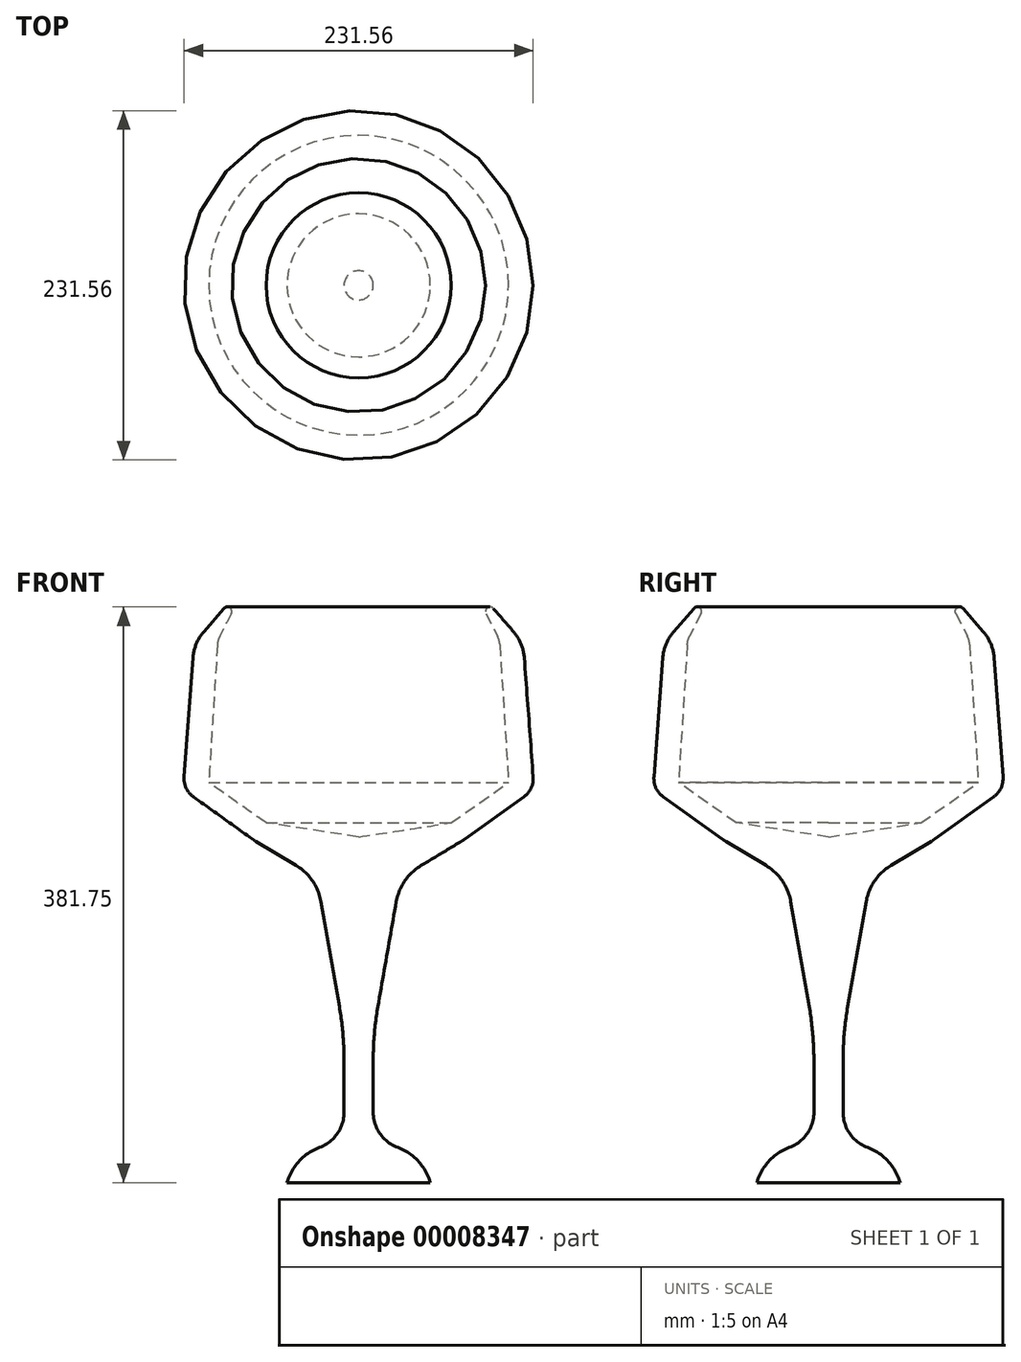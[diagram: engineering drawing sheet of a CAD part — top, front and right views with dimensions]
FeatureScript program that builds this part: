
annotation { "Feature Type Name" : "Feature", "Feature Type Description" : "" }
export const myFeature = defineFeature(function(context is Context, id is Id, definition is map)
    precondition{}
    {
        {
            var Q0;
            Q0=qCreatedBy(makeId("Right.planeOp"),FACE);
            var sketch = newSketch(context, id + "F0", { "sketchPlane" : qUnion([Q0])});
            skLineSegment(sketch, "E0", {"start": v(-9.68, 0) * mm, "end": v(-9.68, -77.4) * mm});
            skLineSegment(sketch, "E1", {"start": v(-9.68, -77.4) * mm, "end": v(-47.46, -77.4) * mm});
            skLineSegment(sketch, "E2", {"start": v(-47.46, -77.4) * mm, "end": v(-47.46, -99.1) * mm});
            skLineSegment(sketch, "E3", {"start": v(-47.46, -99.1) * mm, "end": v(0, -99.1) * mm});
            skLineSegment(sketch, "E4", {"start": v(0, -99.1) * mm, "end": v(0, 130.1) * mm});
            skLineSegment(sketch, "E5", {"start": v(0, 130.1) * mm, "end": v(-61.35, 139.5) * mm});
            skLineSegment(sketch, "E6", {"start": v(-61.35, 139.5) * mm, "end": v(-99.4, 166.13) * mm});
            skLineSegment(sketch, "E7", {"start": v(-99.4, 166.13) * mm, "end": v(-93.44, 260.67) * mm});
            skLineSegment(sketch, "E8", {"start": v(-93.44, 260.67) * mm, "end": v(-73.2, 300.3) * mm});
            skLineSegment(sketch, "E9", {"start": v(-73.2, 300.3) * mm, "end": v(-109.12, 258.83) * mm});
            skLineSegment(sketch, "E10", {"start": v(-109.12, 258.83) * mm, "end": v(-116.36, 161.57) * mm});
            skLineSegment(sketch, "E11", {"start": v(-116.36, 161.57) * mm, "end": v(-69.34, 127.9) * mm});
            skLineSegment(sketch, "E12", {"start": v(-69.34, 127.9) * mm, "end": v(-27.73, 102.92) * mm});
            skLineSegment(sketch, "E13", {"start": v(-27.73, 102.92) * mm, "end": v(-9.68, 0) * mm});
            skLineSegment(sketch, "E14", {"start": v(-47.46, -77.4) * mm, "end": v(-119.56, -99.1) * mm});
            skLineSegment(sketch, "E15", {"start": v(-119.56, -99.1) * mm, "end": v(-47.46, -99.1) * mm});
            skSolve(sketch);
        }
        {
            var Q0;
            Q0=makeQuery(id+"F0.imprint","IMPRINT",FACE,{"disambiguationData":[TD([[makeQuery(id+"F0.imprint","IMPRINT",EDGE,{"derivedFrom":sQuery(id+"F0.wireOp",EDGE,"E0")}),1.0]])]});
            var Q1;
            Q1=sQuery(id+"F0.wireOp",EDGE,"E4");
            revolve(context, id + "F1", {"entities" : qUnion([Q0]), "axis" : qUnion([Q1]), "revolveType" : RevolveType.FULL});
        }
        {
            var Q0;
            Q0=makeQuery(id+"F1.opRevolve","SWEPT_EDGE",EDGE,{"disambiguationData":[OSD([sQuery(id+"F0.wireOp",EDGE,"E8"),sQuery(id+"F0.wireOp",EDGE,"E9")])]});
            fillet(context, id + "F2", {"entities" : qUnion([Q0]), "radius" : 3 * mm, "allowEdgeOverflow" : false});
        }
        {
            var Q0;
            Q0=makeQuery(id+"F1.opRevolve","SWEPT_EDGE",EDGE,{"disambiguationData":[OSD([sQuery(id+"F0.wireOp",EDGE,"E9"),sQuery(id+"F0.wireOp",EDGE,"E10")])]});
            fillet(context, id + "F3", {"entities" : qUnion([Q0]), "radius" : 30 * mm, "allowEdgeOverflow" : false});
        }
        {
            var Q0;
            Q0=makeQuery(id+"F1.opRevolve","SWEPT_EDGE",EDGE,{"disambiguationData":[OSD([sQuery(id+"F0.wireOp",EDGE,"E7"),sQuery(id+"F0.wireOp",EDGE,"E8")])]});
            fillet(context, id + "F4", {"entities" : qUnion([Q0]), "radius" : 15 * mm, "allowEdgeOverflow" : false});
        }
        {
            var Q0;
            Q0=makeQuery(id+"F1.opRevolve","SWEPT_EDGE",EDGE,{"disambiguationData":[OSD([sQuery(id+"F0.wireOp",EDGE,"E10"),sQuery(id+"F0.wireOp",EDGE,"E11")])]});
            fillet(context, id + "F5", {"entities" : qUnion([Q0]), "radius" : 15 * mm, "allowEdgeOverflow" : false});
        }
        {
            var Q0;
            Q0=makeQuery(id+"F1.opRevolve","SWEPT_EDGE",EDGE,{"disambiguationData":[OSD([sQuery(id+"F0.wireOp",EDGE,"E11"),sQuery(id+"F0.wireOp",EDGE,"E12")])]});
            fillet(context, id + "F6", {"entities" : qUnion([Q0]), "radius" : 35 * mm, "tangentPropagation" : true, "allowEdgeOverflow" : false});
        }
        {
            var Q0;
            Q0=makeQuery(id+"F1.opRevolve","SWEPT_EDGE",EDGE,{"disambiguationData":[OSD([sQuery(id+"F0.wireOp",EDGE,"E12"),sQuery(id+"F0.wireOp",EDGE,"E13")])]});
            fillet(context, id + "F7", {"entities" : qUnion([Q0]), "radius" : 35 * mm, "allowEdgeOverflow" : false});
        }
        {
            var Q0;
            Q0=makeQuery(id+"F1.opRevolve","SWEPT_EDGE",EDGE,{"disambiguationData":[OSD([sQuery(id+"F0.wireOp",EDGE,"E0"),sQuery(id+"F0.wireOp",EDGE,"E13")])]});
            fillet(context, id + "F8", {"entities" : qUnion([Q0]), "radius" : 205 * mm, "tangentPropagation" : true, "allowEdgeOverflow" : false});
        }
        {
            var Q0;
            Q0=makeQuery(id+"F1.opRevolve","SWEPT_EDGE",EDGE,{"disambiguationData":[OSD([sQuery(id+"F0.wireOp",EDGE,"E0"),sQuery(id+"F0.wireOp",EDGE,"E1")])]});
            fillet(context, id + "F9", {"entities" : qUnion([Q0]), "radius" : 25 * mm, "tangentPropagation" : true, "allowEdgeOverflow" : false});
        }
        {
            var Q0;
            Q0=makeQuery(id+"F1.opRevolve","SWEPT_EDGE",EDGE,{"disambiguationData":[OSD([sQuery(id+"F0.wireOp",EDGE,"E1"),sQuery(id+"F0.wireOp",EDGE,"E2"),sQuery(id+"F0.wireOp",EDGE,"E14")])]});
            fillet(context, id + "F10", {"entities" : qUnion([Q0]), "radius" : 35 * mm, "tangentPropagation" : true, "allowEdgeOverflow" : false});
        }
    });
